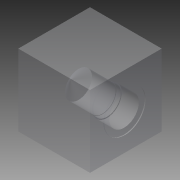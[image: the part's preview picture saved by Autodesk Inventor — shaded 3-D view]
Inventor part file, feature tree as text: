
AUTODESK INVENTOR PART (.ipt)
format: ipt  version: 2014 (Build 180170000, 170)  size: 155,648 bytes
history: native  units: mm
features: other x48, extrude x7, sketch x7
ambient origin geometry x8: Origin, YZ Plane, XZ Plane, XY Plane, X Axis, Y Axis, Z Axis, Center Point
bodies: Body1 (feature_tree)
feature tree (62):
  extrude  "拉伸2"  Depth=19.0mm
  other  "UCS1"
  other  "UCS2"
  other  "UCS3"
  other  "UCS4"
  other  "UCS5"
  other  "UCS6"
  extrude  "拉伸3"  Depth=19.0mm
  extrude  "拉伸4"  Depth=19.0mm
  extrude  "拉伸5"  Depth=1.0mm TaperAngle=0.0deg
  extrude  "拉伸6"  Depth=19.0mm
  extrude  "拉伸7"  Depth=19.0mm TaperAngle=0.0deg
  extrude  "拉伸8"  Depth=19.0mm
  sketch  "草图3"  dims[d39=80.0mm d40=0.0mm]
  sketch  "草图4"  dims[d41=0.0mm d42=0.0mm d43=0.0mm d44=0.0mm d45=0.0mm d46=0.0mm]
  sketch  "草图5"  dims[d47=0.0mm d48=0.0mm d49=0.0mm d50=0.0mm d51=0.0mm d52=0.0mm]
  sketch  "草图6"  dims[d53=0.0mm d54=0.0mm d55=0.0mm d56=0.0mm d57=0.0mm d58=0.0mm]
  sketch  "草图7"  dims[d59=0.0mm d60=0.0mm d61=0.0mm d62=0.0mm d63=0.0mm d64=0.0mm]
  sketch  "草图8"  dims[d65=0.0mm d66=0.0mm d67=0.0mm d68=0.0mm d69=0.0mm d70=0.0mm]
  sketch  "草图9"  dims[d71=0.0mm d72=0.0mm d73=0.0mm d74=0.0mm d75=0.0mm d76=0.0mm d77=46.1mm d78=40.0mm d79=39.0mm d80=1.0mm d81=0.0mm d82=33.0mm d83=19.0mm d84=0.0mm d85=30.75mm d86=24.0mm d87=0.0mm d88=24.0mm d89=-10.297443mm d90=30.0mm d91=50.8mm d92=0.0mm d93=50.8mm d94=-10.297443mm]
  other  "UCS1: YZ 平面"
  other  "UCS1: XZ 平面"
  other  "UCS1: XY 平面"
  other  "UCS1: X 轴"
  other  "UCS1: Y 轴"
  other  "UCS1: Z 轴"
  other  "UCS1: 原点"
  other  "UCS2: YZ 平面"
  other  "UCS2: XZ 平面"
  other  "UCS2: XY 平面"
  other  "UCS2: X 轴"
  other  "UCS2: Y 轴"
  other  "UCS2: Z 轴"
  other  "UCS2: 原点"
  other  "UCS3: YZ 平面"
  other  "UCS3: XZ 平面"
  other  "UCS3: XY 平面"
  other  "UCS3: X 轴"
  other  "UCS3: Y 轴"
  other  "UCS3: Z 轴"
  other  "UCS3: 原点"
  other  "UCS4: YZ 平面"
  other  "UCS4: XZ 平面"
  other  "UCS4: XY 平面"
  other  "UCS4: X 轴"
  other  "UCS4: Y 轴"
  other  "UCS4: Z 轴"
  other  "UCS4: 原点"
  other  "UCS5: YZ 平面"
  other  "UCS5: XZ 平面"
  other  "UCS5: XY 平面"
  other  "UCS5: X 轴"
  other  "UCS5: Y 轴"
  other  "UCS5: Z 轴"
  other  "UCS5: 原点"
  other  "UCS6: YZ 平面"
  other  "UCS6: XZ 平面"
  other  "UCS6: XY 平面"
  other  "UCS6: X 轴"
  other  "UCS6: Y 轴"
  other  "UCS6: Z 轴"
  other  "UCS6: 原点"
